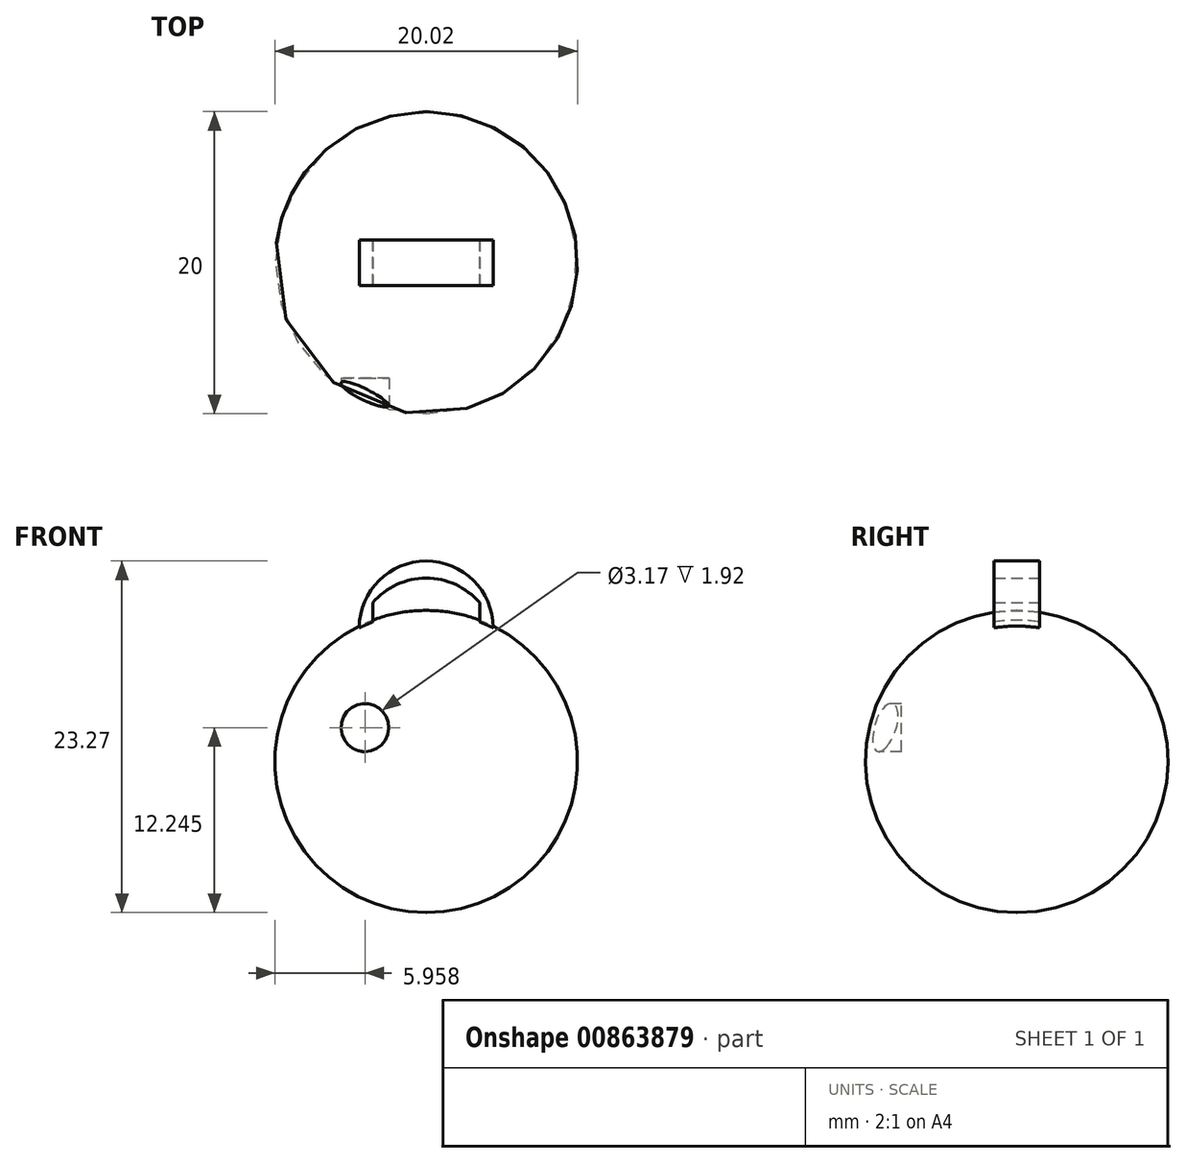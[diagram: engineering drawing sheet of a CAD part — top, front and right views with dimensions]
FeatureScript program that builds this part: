
annotation { "Feature Type Name" : "Feature", "Feature Type Description" : "" }
export const myFeature = defineFeature(function(context is Context, id is Id, definition is map)
    precondition{}
    {
        {
            var Q0;
            Q0=qCreatedBy(makeId("Front.planeOp"),FACE);
            var sketch = newSketch(context, id + "F0", { "sketchPlane" : qUnion([Q0])});
            skLineSegment(sketch, "E0", {"start": v(0, 20.42) * mm, "end": v(0, 0.42) * mm});
            skArc(sketch, "E1", {"start": v(0, 0.42) * mm, "mid": v(10.01, 10.42) * mm, "end": v(0, 20.42) * mm});
            skSolve(sketch);
        }
        {
            var Q0;
            Q0=makeQuery(id+"F0.imprint","IMPRINT",FACE,{"disambiguationData":[TD([[makeQuery(id+"F0.imprint","IMPRINT",EDGE,{"derivedFrom":sQuery(id+"F0.wireOp",EDGE,"E0")}),1.0]])]});
            var Q1;
            Q1=sQuery(id+"F0.wireOp",EDGE,"E0");
            revolve(context, id + "F1", {"surfaceOperationType" : NewSurfaceOperationType.NEW, "entities" : qUnion([Q0]), "axis" : qUnion([Q1]), "revolveType" : RevolveType.FULL});
        }
        {
            var Q0;
            Q0=qCreatedBy(makeId("Front.planeOp"),FACE);
            var sketch = newSketch(context, id + "F2", { "sketchPlane" : qUnion([Q0])});
            skLineSegment(sketch, "E2", {"start": v(-4.43, 19.3) * mm, "end": v(0, 19.3) * mm});
            skLineSegment(sketch, "E3.MirrorCS", {"start": v(4.43, 19.3) * mm, "end": v(0, 19.3) * mm});
            skArc(sketch, "E4", {"start": v(4.43, 19.3) * mm, "mid": v(0, 23.7) * mm, "end": v(-4.43, 19.3) * mm});
            skArc(sketch, "E5", {"start": v(4.43, 19.3) * mm, "mid": v(0, 22.56) * mm, "end": v(-4.43, 19.3) * mm});
            skLineSegment(sketch, "E6", {"start": v(-3.53, 20.93) * mm, "end": v(-3.53, 19.3) * mm});
            skLineSegment(sketch, "E7.MirrorCS", {"start": v(3.53, 20.93) * mm, "end": v(3.53, 19.3) * mm});
            skSolve(sketch);
        }
        {
            var Q0;
            {var subQ0=sQuery(id+"F2.wireOp",EDGE,"E4");Q0=makeQuery(id+"F2.imprint","IMPRINT",FACE,{"disambiguationData":[TD([[makeQuery(id+"F2.imprint","IMPRINT",EDGE,{"derivedFrom":subQ0}),1.0]])]});}
            var Q1;
            {var subQ3=sQuery(id+"F2.wireOp",EDGE,"E6");Q1=makeQuery(id+"F2.imprint","IMPRINT",FACE,{"disambiguationData":[TD([[makeQuery(id+"F2.imprint","IMPRINT",EDGE,{"derivedFrom":subQ3}),-1.0]])]});}
            var Q2;
            {var subQ3=sQuery(id+"F2.wireOp",EDGE,"E7.MirrorCS");Q2=makeQuery(id+"F2.imprint","IMPRINT",FACE,{"disambiguationData":[TD([[makeQuery(id+"F2.imprint","IMPRINT",EDGE,{"derivedFrom":subQ3}),1.0]])]});}
            extrude(context, id + "F3", {"entities" : qUnion([Q0, Q1, Q2]), "operationType" : NewBodyOperationType.ADD, "endBound" : BoundingType.SYMMETRIC, "depth" : 3 * mm, "offsetDistance" : 25.4 * mm});
        }
        {
            var Q0;
            Q0=qCreatedBy(makeId("Front.planeOp"),FACE);
            cPlane(context, id + "F4", {"entities" : qUnion([Q0]), "cplaneType" : CPlaneType.OFFSET, "offset" : 25.4 * mm, "width" : 152.4 * mm, "height" : 152.4 * mm});
        }
        {
            var Q0;
            Q0=qCreatedBy(id+"F4.planeOp",FACE);
            var sketch = newSketch(context, id + "F5", { "sketchPlane" : qUnion([Q0])});
            skCircle(sketch, "E8", {"center": v(-4.05, 12.67) * mm, "radius": 1.59 * mm});
            skCircle(sketch, "E9.MirrorC", {"center": v(4.05, 12.67) * mm, "radius": 1.59 * mm});
            skSolve(sketch);
        }
        {
            var Q0;
            Q0=makeQuery(id+"F5.imprint","IMPRINT",FACE,{"disambiguationData":[TD([[makeQuery(id+"F5.imprint","IMPRINT",EDGE,{"derivedFrom":sQuery(id+"F5.wireOp",EDGE,"E8")}),1.0]])]});
            var Q1;
            Q1=makeQuery(id+"F5.imprint","IMPRINT",FACE,{"disambiguationData":[TD([[makeQuery(id+"F5.imprint","IMPRINT",EDGE,{"derivedFrom":sQuery(id+"F5.wireOp",EDGE,"E9.MirrorC")}),-1.0]])]});
            extrude(context, id + "F6", {"entities" : qUnion([Q0, Q1]), "operationType" : NewBodyOperationType.REMOVE, "oppositeDirection" : true, "depth" : 17.78 * mm, "offsetDistance" : 25.4 * mm});
        }
    });
